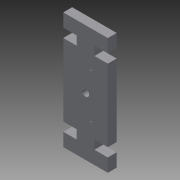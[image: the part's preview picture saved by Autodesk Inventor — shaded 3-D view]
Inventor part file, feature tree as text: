
AUTODESK INVENTOR PART (.ipt)
format: ipt  version: 2015 (Build 190159000, 159)  size: 116,736 bytes
history: native  units: mm
features: extrude x3, sketch x2
ambient origin geometry x8: Origin, YZ Plane, XZ Plane, XY Plane, X Axis, Y Axis, Z Axis, Center Point
bodies: Solid1 (feature_tree)
feature tree (5):
  sketch  "Sketch1"  dims[d0=50.0mm d1=131.0mm]
  extrude  "Extrusion1"  Depth=131.0mm
  extrude  "Extrusion2"  Depth=10.0mm
  extrude  "Extrusion4"  Depth=10.0mm
  sketch  "Sketch3"  dims[d2=10.0mm d3=0.0mm d4=8.0mm d10=2.0mm d11=10.0mm d12=0.0mm d18=14.9mm d19=15.0mm d20=24.9mm d21=15.0mm d22=24.9mm d24=14.9mm d25=15.0mm d26=24.9mm d28=14.9mm d29=15.0mm d30=24.9mm d32=14.9mm d34=2.5mm d35=10.0mm d36=0.0mm]
